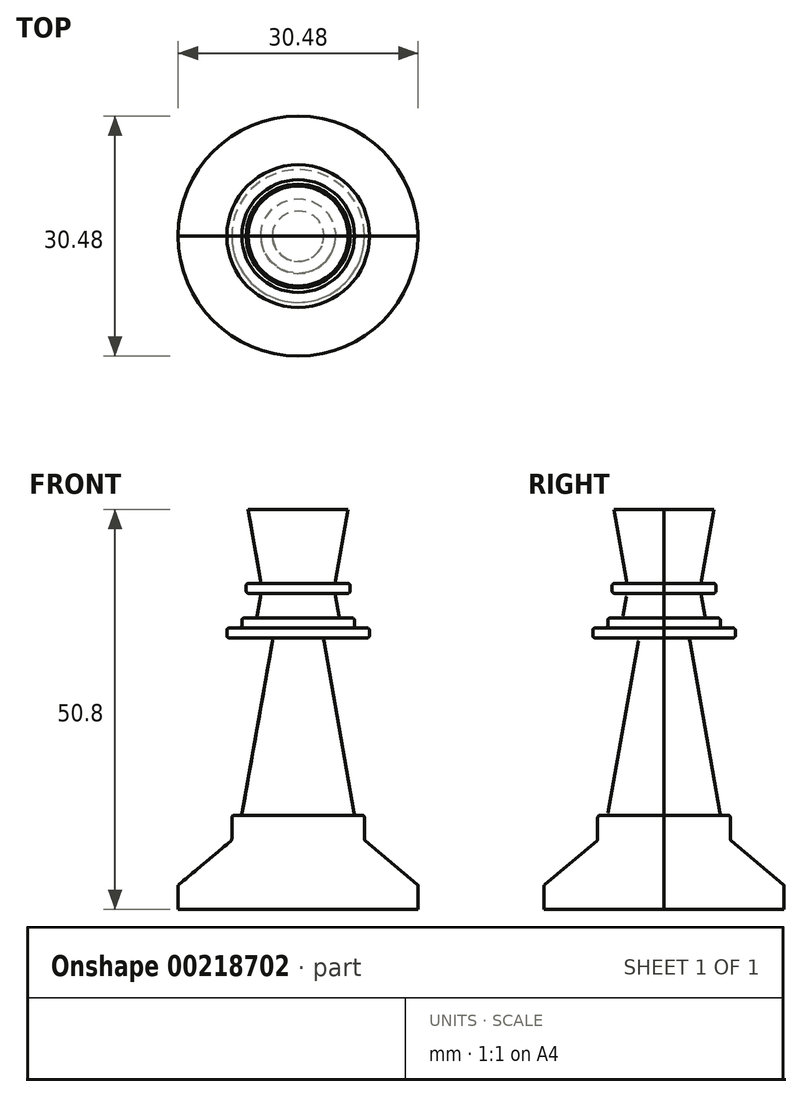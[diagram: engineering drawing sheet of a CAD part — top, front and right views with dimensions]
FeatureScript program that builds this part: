
annotation { "Feature Type Name" : "Feature", "Feature Type Description" : "" }
export const myFeature = defineFeature(function(context is Context, id is Id, definition is map)
    precondition{}
    {
        {
            var Q0;
            Q0=qCreatedBy(makeId("Front.planeOp"),FACE);
            var sketch = newSketch(context, id + "F0", { "sketchPlane" : qUnion([Q0])});
            skLineSegment(sketch, "E0.bottom", {"start": v(0, 0) * mm, "end": v(-15.24, 0) * mm});
            skLineSegment(sketch, "E0.top", {"start": v(0, 50.8) * mm, "end": v(-6.35, 50.8) * mm});
            skLineSegment(sketch, "E0.left", {"start": v(0, 0) * mm, "end": v(0, 50.8) * mm});
            skLineSegment(sketch, "E1", {"start": v(-15.24, 0) * mm, "end": v(-15.24, 2.93) * mm});
            skLineSegment(sketch, "E2", {"start": v(-15.13, 3.18) * mm, "end": v(-8.54, 8.7) * mm});
            skLineSegment(sketch, "E3", {"start": v(-8.43, 8.94) * mm, "end": v(-8.43, 11.65) * mm});
            skLineSegment(sketch, "E4", {"start": v(-8.11, 11.97) * mm, "end": v(-7.43, 11.97) * mm});
            skLineSegment(sketch, "E5", {"start": v(-7.11, 12.23) * mm, "end": v(-3.26, 34.11) * mm});
            skLineSegment(sketch, "E6", {"start": v(-3.57, 34.48) * mm, "end": v(-8.74, 34.48) * mm});
            skLineSegment(sketch, "E7", {"start": v(-9.06, 34.8) * mm, "end": v(-9.06, 35.44) * mm});
            skLineSegment(sketch, "E8", {"start": v(-8.74, 35.75) * mm, "end": v(-7.47, 35.75) * mm});
            skLineSegment(sketch, "E9", {"start": v(-7.15, 36.07) * mm, "end": v(-7.15, 36.7) * mm});
            skLineSegment(sketch, "E10", {"start": v(-6.83, 37.02) * mm, "end": v(-5.51, 37.02) * mm});
            skLineSegment(sketch, "E11", {"start": v(-5.2, 37.29) * mm, "end": v(-4.76, 39.78) * mm});
            skLineSegment(sketch, "E12", {"start": v(-5.07, 40.15) * mm, "end": v(-6.28, 40.15) * mm});
            skLineSegment(sketch, "E13", {"start": v(-6.6, 40.47) * mm, "end": v(-6.6, 41.1) * mm});
            skLineSegment(sketch, "E14", {"start": v(-6.28, 41.42) * mm, "end": v(-5.07, 41.42) * mm});
            skLineSegment(sketch, "E15", {"start": v(-4.76, 41.8) * mm, "end": v(-6.35, 50.8) * mm});
            skPoint(sketch, "E16.visualSharp", {"position": v(-15.24, 3.08) * mm});
            skArc(sketch, "E16.filletArc", {"start": v(-15.13, 3.18) * mm, "mid": v(-15.21, 3.07) * mm, "end": v(-15.24, 2.93) * mm});
            skPoint(sketch, "E17.visualSharp", {"position": v(-8.43, 8.8) * mm});
            skArc(sketch, "E17.filletArc", {"start": v(-8.54, 8.7) * mm, "mid": v(-8.46, 8.8) * mm, "end": v(-8.43, 8.94) * mm});
            skPoint(sketch, "E18.visualSharp", {"position": v(-3.2, 34.48) * mm});
            skArc(sketch, "E18.filletArc", {"start": v(-3.26, 34.11) * mm, "mid": v(-3.33, 34.37) * mm, "end": v(-3.57, 34.48) * mm});
            skPoint(sketch, "E19.visualSharp", {"position": v(-8.43, 11.97) * mm});
            skArc(sketch, "E19.filletArc", {"start": v(-8.11, 11.97) * mm, "mid": v(-8.34, 11.88) * mm, "end": v(-8.43, 11.65) * mm});
            skPoint(sketch, "E20.visualSharp", {"position": v(-7.16, 11.97) * mm});
            skArc(sketch, "E20.filletArc", {"start": v(-7.43, 11.97) * mm, "mid": v(-7.22, 12.04) * mm, "end": v(-7.11, 12.23) * mm});
            skPoint(sketch, "E21.visualSharp", {"position": v(-9.06, 34.48) * mm});
            skArc(sketch, "E21.filletArc", {"start": v(-9.06, 34.8) * mm, "mid": v(-8.96, 34.58) * mm, "end": v(-8.74, 34.48) * mm});
            skPoint(sketch, "E22.visualSharp", {"position": v(-9.06, 35.75) * mm});
            skArc(sketch, "E22.filletArc", {"start": v(-8.74, 35.75) * mm, "mid": v(-8.96, 35.66) * mm, "end": v(-9.06, 35.44) * mm});
            skPoint(sketch, "E23.visualSharp", {"position": v(-7.15, 35.75) * mm});
            skArc(sketch, "E23.filletArc", {"start": v(-7.47, 35.75) * mm, "mid": v(-7.25, 35.85) * mm, "end": v(-7.15, 36.07) * mm});
            skPoint(sketch, "E24.visualSharp", {"position": v(-7.15, 37.02) * mm});
            skArc(sketch, "E24.filletArc", {"start": v(-6.83, 37.02) * mm, "mid": v(-7.06, 36.93) * mm, "end": v(-7.15, 36.7) * mm});
            skPoint(sketch, "E25.visualSharp", {"position": v(-5.25, 37.02) * mm});
            skArc(sketch, "E25.filletArc", {"start": v(-5.51, 37.02) * mm, "mid": v(-5.3, 37.1) * mm, "end": v(-5.2, 37.29) * mm});
            skPoint(sketch, "E26.visualSharp", {"position": v(-4.7, 40.15) * mm});
            skArc(sketch, "E26.filletArc", {"start": v(-4.76, 39.78) * mm, "mid": v(-4.83, 40.04) * mm, "end": v(-5.07, 40.15) * mm});
            skPoint(sketch, "E27.visualSharp", {"position": v(-6.6, 40.15) * mm});
            skArc(sketch, "E27.filletArc", {"start": v(-6.6, 40.47) * mm, "mid": v(-6.5, 40.24) * mm, "end": v(-6.28, 40.15) * mm});
            skPoint(sketch, "E28.visualSharp", {"position": v(-6.6, 41.42) * mm});
            skArc(sketch, "E28.filletArc", {"start": v(-6.28, 41.42) * mm, "mid": v(-6.5, 41.33) * mm, "end": v(-6.6, 41.1) * mm});
            skPoint(sketch, "E29.visualSharp", {"position": v(-4.7, 41.42) * mm});
            skArc(sketch, "E29.filletArc", {"start": v(-5.07, 41.42) * mm, "mid": v(-4.83, 41.53) * mm, "end": v(-4.76, 41.8) * mm});
            skSolve(sketch);
        }
        {
            var Q0;
            Q0=makeQuery(id+"F0.imprint","IMPRINT",FACE,{"disambiguationData":[TD([[makeQuery(id+"F0.imprint","IMPRINT",EDGE,{"derivedFrom":sQuery(id+"F0.wireOp",EDGE,"E0.bottom")}),-1.0]])]});
            var Q1;
            Q1=sQuery(id+"F0.wireOp",EDGE,"E0.left");
            revolve(context, id + "F1", {"entities" : qUnion([Q0]), "axis" : qUnion([Q1]), "revolveType" : RevolveType.ONE_DIRECTION, "angle" : 180 * degree});
        }
        {
            var Q0;
            Q0=makeQuery(id+"F0.imprint","IMPRINT",FACE,{"disambiguationData":[TD([[makeQuery(id+"F0.imprint","IMPRINT",EDGE,{"derivedFrom":sQuery(id+"F0.wireOp",EDGE,"E0.bottom")}),-1.0]])]});
            var Q1;
            Q1=sQuery(id+"F0.wireOp",EDGE,"E0.left");
            revolve(context, id + "F2", {"entities" : qUnion([Q0]), "axis" : qUnion([Q1]), "revolveType" : RevolveType.FULL});
        }
    });
